# Revit family: SIMES_S.1220W_Stage
name_source: partatom
category: Lighting Fixtures
revit_build: Autodesk Revit 2016 (Build: 20150714_1515(x64)
units: mm (PartAtom-declared; Revit-internal decimal feet)

## family parameters
Cut with Voids When Loaded = No
Host = Face
Light Source = No
OmniClass Number = 23.80.70.14
OmniClass Title = Luminaries for External Lighting
Part Type = Normal
Room Calculation Point = No
Round Connector Dimension = Use Diameter
Shared = No

## types (1)
- SIMES_S.1220W_Stage
    Approval mark = CE
    Assembly Code = D5020
    Color Rendering Index = CRI 80
    Colour Temperature = 3000
    Control Gear = electronic transformer
    Default Elevation = 1219 mm
    Description = MINISTAGE
Art. S.1220W
MODULES LED COB 3000K  230V CRI 80
Rated luminaire luminous flux: 4336lm
Rated input power: 40W
Luminaire efficacy: 108lm/W
Electronic ballast 220÷240V 50/60Hz
CE

Fixture available with integral DALI driver on request with surcharge.

PRODUCT TYPE
Projector. IP rating IP 65
MATERIAL CHARACTERISTICS
Die-cast EN AB-47100 aluminium housing with high corrosion resistance.
Stone wash surface treatment prior to painting process. A4 grade Stainless Steel screws with 2,5-3% molybdenum content which increases the resistance against corrosion. Silicone gaskets. Painting Process : 3 Step Process
1) Surface treatment with BONDERITE. A heavy metal free chemical surface treatment containing ceramic nano particles giving a cohesive, inorganic and highly dense protective coating. 2) PRE POLYMERIZATION a process of introducing an epoxy primer with excellent characteristics to the paint which also offers very high resistance to oxidation due to its Zinc content. 3) POLYMERIZATION a process with the application of polyester powder with high resistance against UV rays and harsh weather conditions. Resistance test protection for Marine applications for 1200h.  Mechanical resistance IK 06
LIGHTING PERFORMANCE
Asymmetrical optics: The scoop optic of the asymmetrical version assures a high visual comfort avoiding the direct visibility of the LED source that normally has a high glaring luminance.
Symmetrical optics: The 19° and 37° narrow and medium beams  with symmetrical optics, are obtained through the use of mid power  COB in combination with high performance lenses.
Flood beam: 99.98% pure aluminium reflectors. Clear toughened glass. 
LOR -- 
INSTALLATION AND MAINTENANCE
The tempered front glass diffuser is fixed externally to the fitting through silicon resin, perfectly flush with the front ring. Water and dirt deposits that can disturb the lighting performance of the projector can easily flow away. 
WIRING
Luminaire suitable for double cable glands.  Isolation: CLASS II . Available colours: Aluminium grey (cod.14). Weight: 5.2 Kg Glow Wire test: --
Lamp included.
REGISTERED DESIGN
This luminaire contains built-in LED modules with energy class: A, A+, A++. In case of damage or malfunction please contact the manufacturer to receive additional instructions on how to replace and relative spare parts to order. The LED modules cannot be handled in the luminaire by the end user (Regulation UE 874/2012).
LED circuit boards are engineered accordingly to actual Lumen Maintenance regulation (LM80) and Technical Memorandum (TM21) where uniformity and quality of light is 50.000 hours referred to L70  B20 Ta 25°C.Lifecycle refers to LED circuit boards only, all others components of the luminaire are excluded.
    Frequency = 50/60Hz
    IFC Classification = Light Fixture
    IK Rating = IK 06
    Lamp = LED
    Lamp Light Flux = 5319
    Lamp Power = 15,800000190734863
    Lamp count = 1
    Last Update = 08/11/2018 15:58:25
    Lifetime = 50000 L70 B20 Ta 25°C
    Light Output Ratio = 100
    Luminous efficacy = 108,4
    Manufacturer = SIMES
    Masterformat 2014 Code = 26 56 00
    Masterformat 2014 Description = Exterior Lighting
    Model = S.1220W
    Mounting Place = Wall
    Mounting Type = Surface mounted
    NBS Reference Code = 49
    NBS Reference Description = Luminaries And Lamps
    OmniClass Code = 23-35 47 11
    OmniClass Description = Lighting Fixture
    Product Group = projector
    Product Name = Stage
    Protection Class = Protection class II
    Protection Degree = IP 65
    System Light Flux = 4336
    System Power = 40
    Type Comments = SIMES S.p.A. - All rights reserved
    Type Image = stage_mini_simmetrico.jpg
    UNSPSC Code = 3911
    URL = http://www.simes.it
    Uniclass 1.4 Code = YJ73
    Uniclass 1.4 Description = Luminaries and lamps
    Uniclass 2.0 Code = PR-49
    Uniclass 2.0 Description = Luminaries and lamps
    Uniclass 2015 Code = EF_70_80
    Uniclass 2015 Name = Lighting
    Uniformat II Code = D5020
    Uniformat II Description = Lighting & Branch Wiring
    Voltage = 220÷240V
    Wattage Comments = 84W

## geometry (parser evidence)
native form markers: Blend x2, Sweep x3
no freeform markers — native parametric forms only
